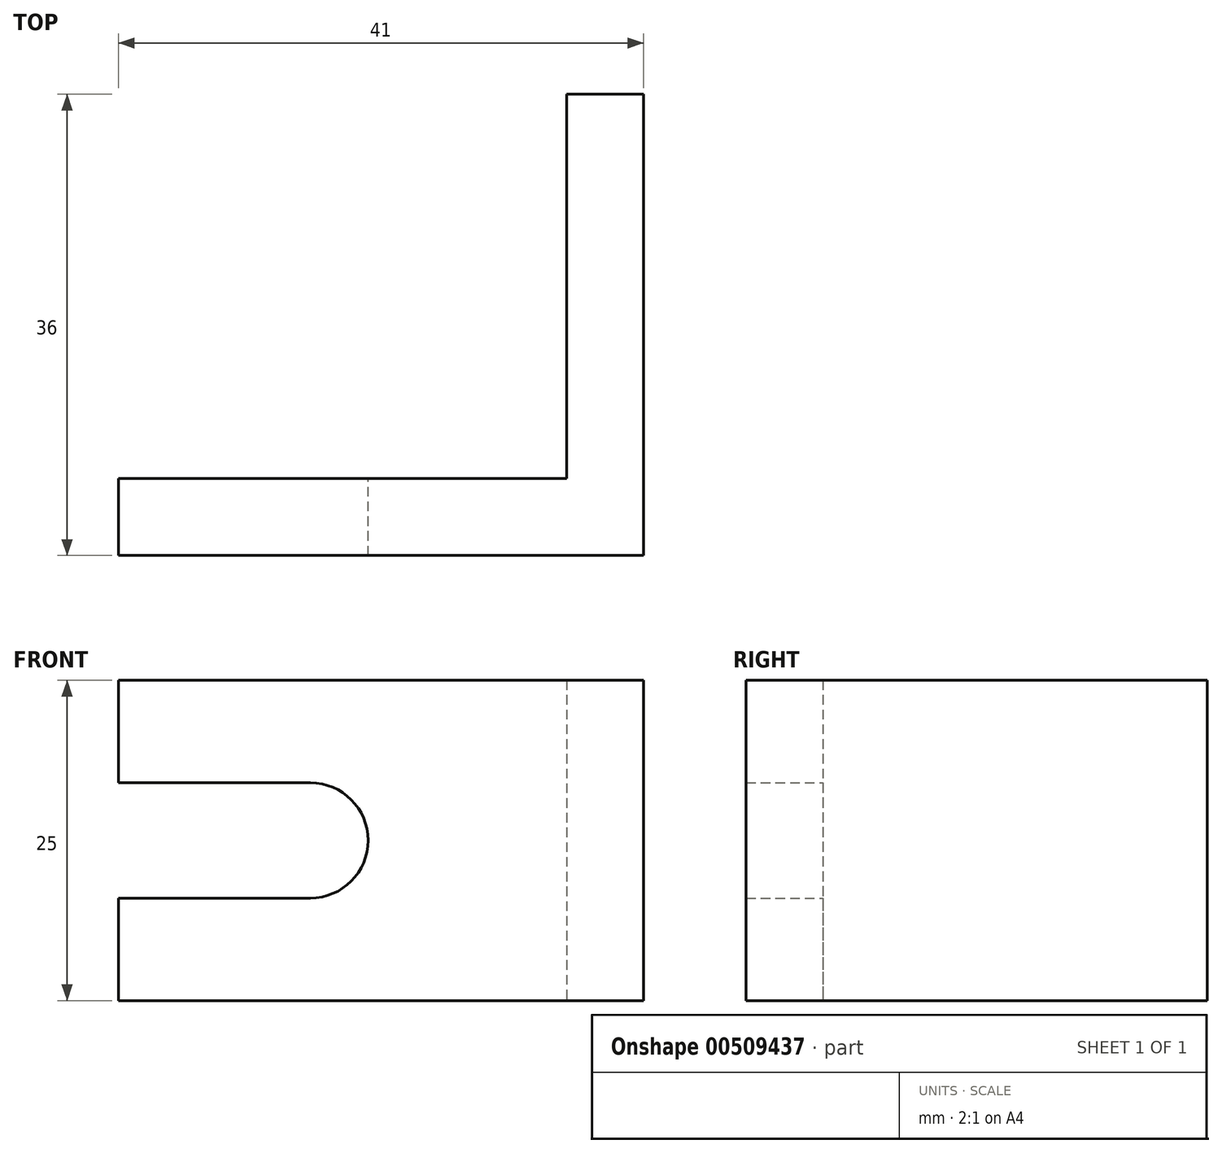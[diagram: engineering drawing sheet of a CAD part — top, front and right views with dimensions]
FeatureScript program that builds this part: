
annotation { "Feature Type Name" : "Feature", "Feature Type Description" : "" }
export const myFeature = defineFeature(function(context is Context, id is Id, definition is map)
    precondition{}
    {
        {
            var Q0;
            Q0=qCreatedBy(makeId("Top.planeOp"),FACE);
            var sketch = newSketch(context, id + "F0", { "sketchPlane" : qUnion([Q0])});
            skLineSegment(sketch, "E0.right", {"start": v(-11, 3) * mm, "end": v(-11, -3) * mm});
            skPoint(sketch, "E0.middle", {"position": v(0, 0) * mm});
            skLineSegment(sketch, "E1.top", {"start": v(-11, -33) * mm, "end": v(-5, -33) * mm});
            skLineSegment(sketch, "E1.left", {"start": v(-11, -3) * mm, "end": v(-11, -33) * mm});
            skLineSegment(sketch, "E2.top", {"start": v(11, -33) * mm, "end": v(5, -33) * mm});
            skLineSegment(sketch, "E3.bottom", {"start": v(-11, -33) * mm, "end": v(-46, -33) * mm});
            skLineSegment(sketch, "E3.top", {"start": v(-11, -27) * mm, "end": v(-46, -27) * mm});
            skLineSegment(sketch, "E3.left", {"start": v(-11, -33) * mm, "end": v(-11, -27) * mm});
            skLineSegment(sketch, "E3.right", {"start": v(-46, -33) * mm, "end": v(-46, -27) * mm});
            skLineSegment(sketch, "E4", {"start": v(-5, -33) * mm, "end": v(-5, -3) * mm});
            skLineSegment(sketch, "E5", {"start": v(-5, -3) * mm, "end": v(-5, 3) * mm});
            skLineSegment(sketch, "E6", {"start": v(-11, 3) * mm, "end": v(-5, 3) * mm});
            skSolve(sketch);
        }
        {
            var Q0;
            Q0=makeQuery(id+"F0.imprint","IMPRINT",FACE,{"disambiguationData":[TD([[makeQuery(id+"F0.imprint","IMPRINT",EDGE,{"derivedFrom":sQuery(id+"F0.wireOp",EDGE,"E3.bottom")}),-1.0]])]});
            var Q1;
            Q1=makeQuery(id+"F0.imprint","IMPRINT",FACE,{"disambiguationData":[TD([[makeQuery(id+"F0.imprint","IMPRINT",EDGE,{"derivedFrom":sQuery(id+"F0.wireOp",EDGE,"E1.top")}),1.0]])]});
            var Q2;
            Q2=makeQuery(id+"F0.imprint","IMPRINT",FACE,{"disambiguationData":[TD([[makeQuery(id+"F0.imprint","IMPRINT",EDGE,{"derivedFrom":sQuery(id+"F0.wireOp",EDGE,"E0.bottom")}),1.0]])]});
            var Q3;
            Q3=makeQuery(id+"F0.imprint","IMPRINT",FACE,{"disambiguationData":[TD([[makeQuery(id+"F0.imprint","IMPRINT",EDGE,{"derivedFrom":sQuery(id+"F0.wireOp",EDGE,"E2.top")}),-1.0]])]});
            extrude(context, id + "F1", {"entities" : qUnion([Q0, Q1, Q2, Q3]), "depth" : 25 * mm});
        }
        {
            var Q0;
            Q0=makeQuery(id+"F1.opExtrude","SWEPT_FACE",FACE,{"disambiguationData":[OSD([sQuery(id+"F0.wireOp",EDGE,"E3.top")])]});
            var sketch = newSketch(context, id + "F2", { "sketchPlane" : qUnion([Q0])});
            skCircle(sketch, "E7", {"center": v(31, 12.5) * mm, "radius": 4.5 * mm});
            skLineSegment(sketch, "E8", {"start": v(31, 17) * mm, "end": v(46, 17) * mm});
            skLineSegment(sketch, "E9", {"start": v(31, 8) * mm, "end": v(46, 8) * mm});
            skSolve(sketch);
        }
        {
            var Q0;
            Q0=makeQuery(id+"F2.imprint","IMPRINT",FACE,{"disambiguationData":[TD([[makeQuery(id+"F2.imprint","IMPRINT",EDGE,{"derivedFrom":sQuery(id+"F2.wireOp",EDGE,"E7")}),1.0]])]});
            extrude(context, id + "F3", {"entities" : qUnion([Q0]), "operationType" : NewBodyOperationType.REMOVE, "oppositeDirection" : true, "depth" : 25 * mm});
        }
        {
            var Q0;
            {var subQ0=sQuery(id+"F2.wireOp",EDGE,"E8");Q0=makeQuery(id+"F2.imprint","IMPRINT",FACE,{"disambiguationData":[TD([[makeQuery(id+"F2.imprint","IMPRINT",EDGE,{"derivedFrom":subQ0}),-1.0]])]});}
            extrude(context, id + "F4", {"entities" : qUnion([Q0]), "operationType" : NewBodyOperationType.REMOVE, "oppositeDirection" : true, "depth" : 25 * mm});
        }
    });
